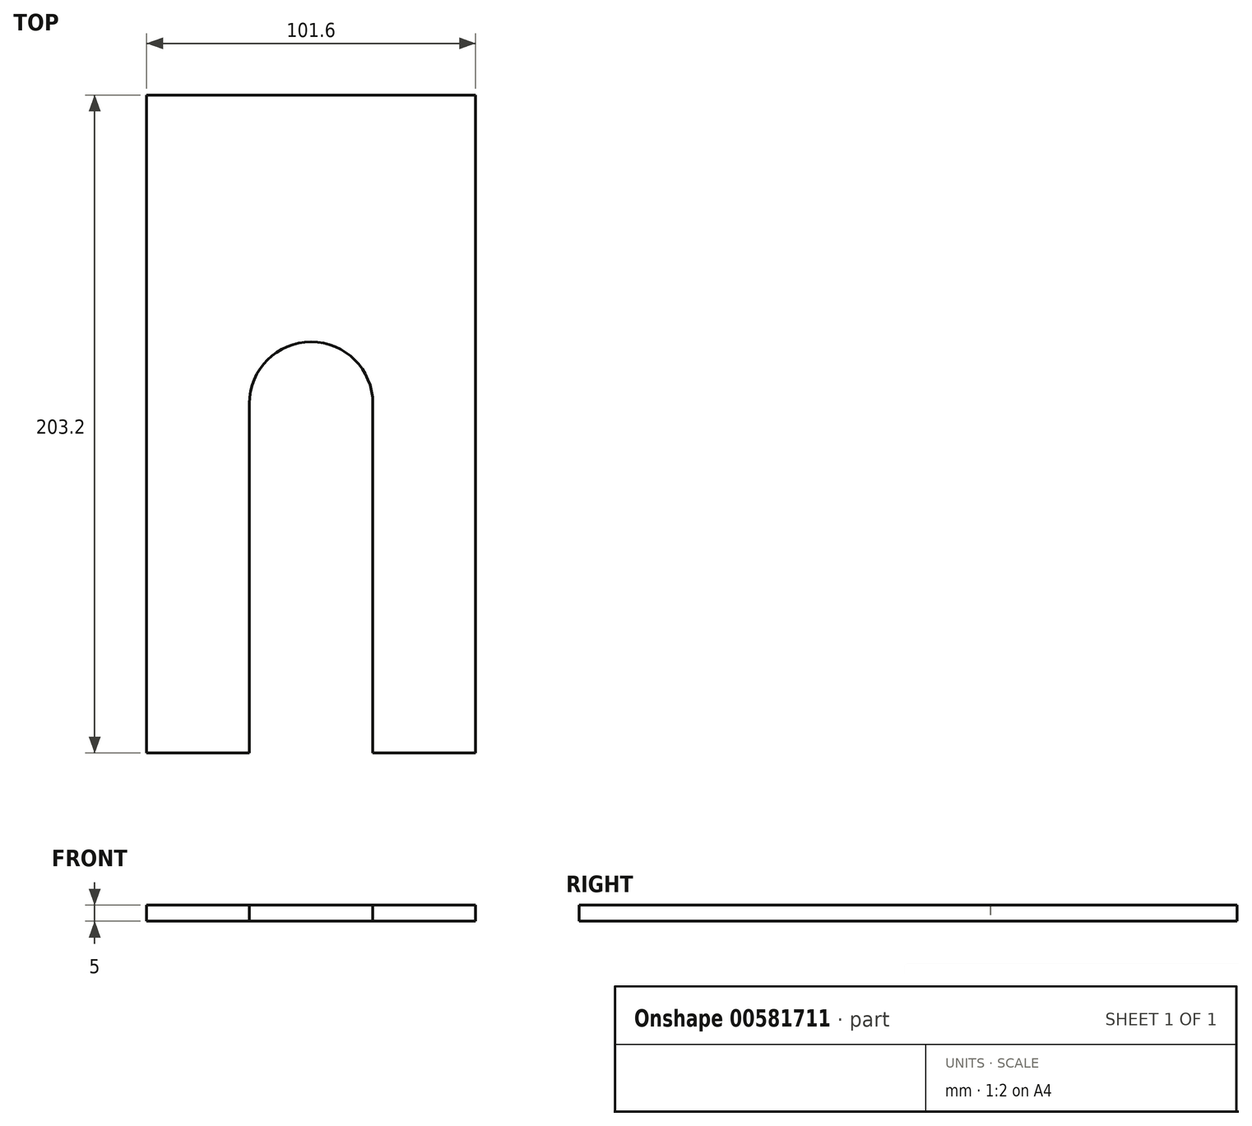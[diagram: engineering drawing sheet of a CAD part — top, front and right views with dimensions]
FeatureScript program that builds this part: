
annotation { "Feature Type Name" : "Feature", "Feature Type Description" : "" }
export const myFeature = defineFeature(function(context is Context, id is Id, definition is map)
    precondition{}
    {
        {
            var Q0;
            Q0=qCreatedBy(makeId("Top.planeOp"),FACE);
            var sketch = newSketch(context, id + "F0", { "sketchPlane" : qUnion([Q0])});
            skLineSegment(sketch, "E0.bottom", {"start": v(-42.57, 111.85) * mm, "end": v(33.63, 111.85) * mm});
            skLineSegment(sketch, "E0.top", {"start": v(-42.57, -91.35) * mm, "end": v(33.63, -91.35) * mm});
            skLineSegment(sketch, "E0.left", {"start": v(-42.57, 111.85) * mm, "end": v(-42.57, -91.35) * mm});
            skLineSegment(sketch, "E0.right", {"start": v(33.63, 111.85) * mm, "end": v(33.63, -91.35) * mm});
            skLineSegment(sketch, "E1.bottom", {"start": v(-23.52, -91.35) * mm, "end": v(14.58, -91.35) * mm});
            skLineSegment(sketch, "E1.top", {"start": v(-23.52, 35.65) * mm, "end": v(14.58, 35.65) * mm});
            skLineSegment(sketch, "E1.left", {"start": v(-23.52, -91.35) * mm, "end": v(-23.52, 35.65) * mm});
            skLineSegment(sketch, "E1.right", {"start": v(14.58, -91.35) * mm, "end": v(14.58, 35.65) * mm});
            skPoint(sketch, "E2", {"position": v(-4.47, -91.35) * mm});
            skArc(sketch, "E3", {"start": v(14.58, 16.6) * mm, "mid": v(-4.47, 35.65) * mm, "end": v(-23.52, 16.6) * mm});
            skLineSegment(sketch, "E4.bottom", {"start": v(33.63, 111.85) * mm, "end": v(46.33, 111.85) * mm});
            skLineSegment(sketch, "E4.top", {"start": v(33.63, -91.35) * mm, "end": v(46.33, -91.35) * mm});
            skLineSegment(sketch, "E4.right", {"start": v(46.33, 111.85) * mm, "end": v(46.33, -91.35) * mm});
            skLineSegment(sketch, "E5.bottom", {"start": v(-42.57, 111.85) * mm, "end": v(-55.27, 111.85) * mm});
            skLineSegment(sketch, "E5.top", {"start": v(-42.57, -91.35) * mm, "end": v(-55.27, -91.35) * mm});
            skLineSegment(sketch, "E5.right", {"start": v(-55.27, 111.85) * mm, "end": v(-55.27, -91.35) * mm});
            skSolve(sketch);
        }
        {
            var Q0;
            Q0=makeQuery(id+"F0.imprint","IMPRINT",FACE,{"disambiguationData":[TD([[makeQuery(id+"F0.imprint","IMPRINT",EDGE,{"derivedFrom":sQuery(id+"F0.wireOp",EDGE,"E0.bottom")}),-1.0]])]});
            var Q1;
            {var subQ0=sQuery(id+"F0.wireOp",EDGE,"E1.right");var subQ1=sQuery(id+"F0.wireOp",EDGE,"E1.top");var subQ2=makeQuery(id+"F0.imprint","INTERSECT",VERTEX,{"derivedFrom":[subQ1,subQ0]});Q1=makeQuery(id+"F0.imprint","IMPRINT",FACE,{"disambiguationData":[TD([[makeQuery(id+"F0.imprint","IMPRINT",EDGE,{"disambiguationData":[TD([[subQ2,1.0]])],"derivedFrom":subQ1}),-1.0]])]});}
            var Q2;
            {var subQ0=sQuery(id+"F0.wireOp",EDGE,"E1.left");var subQ1=sQuery(id+"F0.wireOp",EDGE,"E1.top");var subQ2=makeQuery(id+"F0.imprint","INTERSECT",VERTEX,{"derivedFrom":[subQ1,subQ0]});Q2=makeQuery(id+"F0.imprint","IMPRINT",FACE,{"disambiguationData":[TD([[makeQuery(id+"F0.imprint","IMPRINT",EDGE,{"disambiguationData":[TD([[subQ2,-1.0]])],"derivedFrom":subQ1}),-1.0]])]});}
            var Q3;
            Q3=makeQuery(id+"F0.imprint","IMPRINT",FACE,{"disambiguationData":[TD([[makeQuery(id+"F0.imprint","IMPRINT",EDGE,{"derivedFrom":sQuery(id+"F0.wireOp",EDGE,"E5.bottom")}),1.0]])]});
            var Q4;
            Q4=makeQuery(id+"F0.imprint","IMPRINT",FACE,{"disambiguationData":[TD([[makeQuery(id+"F0.imprint","IMPRINT",EDGE,{"derivedFrom":sQuery(id+"F0.wireOp",EDGE,"E4.bottom")}),-1.0]])]});
            extrude(context, id + "F1", {"entities" : qUnion([Q0, Q1, Q2, Q3, Q4]), "depth" : 5 * mm, "offsetDistance" : 25 * mm});
        }
    });
